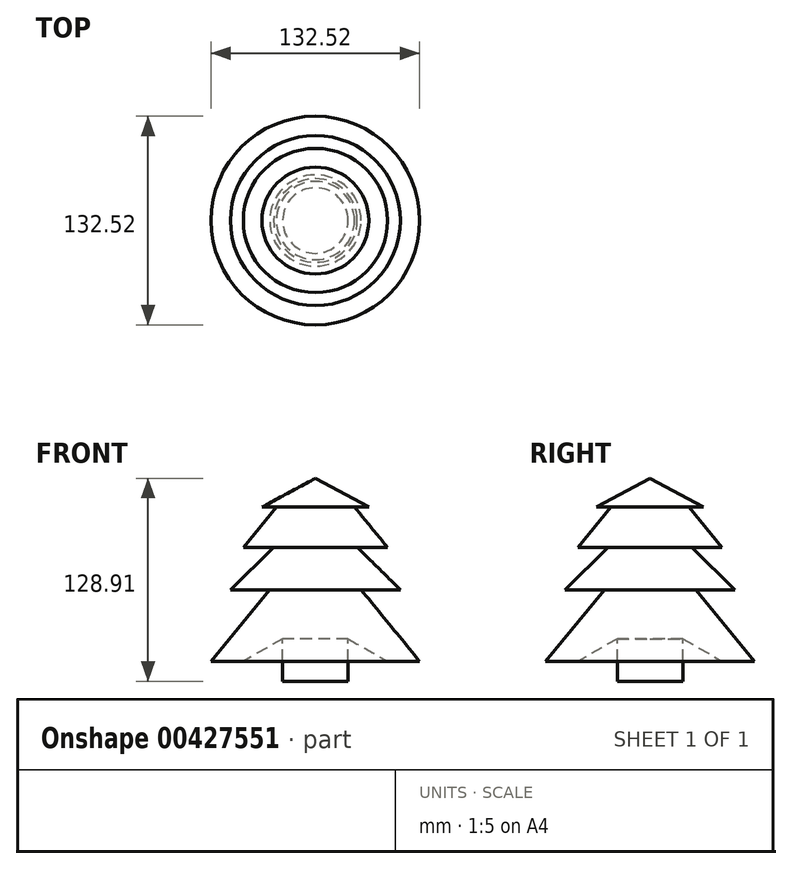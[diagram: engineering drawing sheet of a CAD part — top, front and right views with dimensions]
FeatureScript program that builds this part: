
annotation { "Feature Type Name" : "Feature", "Feature Type Description" : "" }
export const myFeature = defineFeature(function(context is Context, id is Id, definition is map)
    precondition{}
    {
        {
            var Q0;
            Q0=qCreatedBy(makeId("Front.planeOp"),FACE);
            var sketch = newSketch(context, id + "F0", { "sketchPlane" : qUnion([Q0])});
            skLineSegment(sketch, "E0", {"start": v(0, 56.35) * mm, "end": v(0, -72.56) * mm});
            skLineSegment(sketch, "E1", {"start": v(0, -72.56) * mm, "end": v(20.84, -72.56) * mm});
            skLineSegment(sketch, "E2", {"start": v(20.84, -72.56) * mm, "end": v(20.84, -45.55) * mm});
            skLineSegment(sketch, "E3", {"start": v(20.84, -45.55) * mm, "end": v(45.8, -59.87) * mm});
            skLineSegment(sketch, "E4", {"start": v(45.8, -59.87) * mm, "end": v(66.26, -59.87) * mm});
            skLineSegment(sketch, "E5", {"start": v(66.26, -59.87) * mm, "end": v(29.02, -14.45) * mm});
            skLineSegment(sketch, "E6", {"start": v(29.02, -14.45) * mm, "end": v(53.98, -14.45) * mm});
            skLineSegment(sketch, "E7", {"start": v(53.98, -14.45) * mm, "end": v(26.56, 12.56) * mm});
            skLineSegment(sketch, "E8", {"start": v(26.56, 12.56) * mm, "end": v(45.8, 12.56) * mm});
            skLineSegment(sketch, "E9", {"start": v(45.8, 12.56) * mm, "end": v(24.84, 38.12) * mm});
            skLineSegment(sketch, "E10", {"start": v(24.84, 38.12) * mm, "end": v(33.93, 38.12) * mm});
            skLineSegment(sketch, "E11", {"start": v(33.93, 38.12) * mm, "end": v(0, 56.35) * mm});
            skSolve(sketch);
        }
        {
            var Q0;
            Q0 = qSketchRegion(id + "F0", true);
            var Q1;
            Q1=sQuery(id+"F0.wireOp",EDGE,"E0");
            revolve(context, id + "F1", {"entities" : qUnion([Q0]), "axis" : qUnion([Q1]), "revolveType" : RevolveType.FULL});
        }
    });
